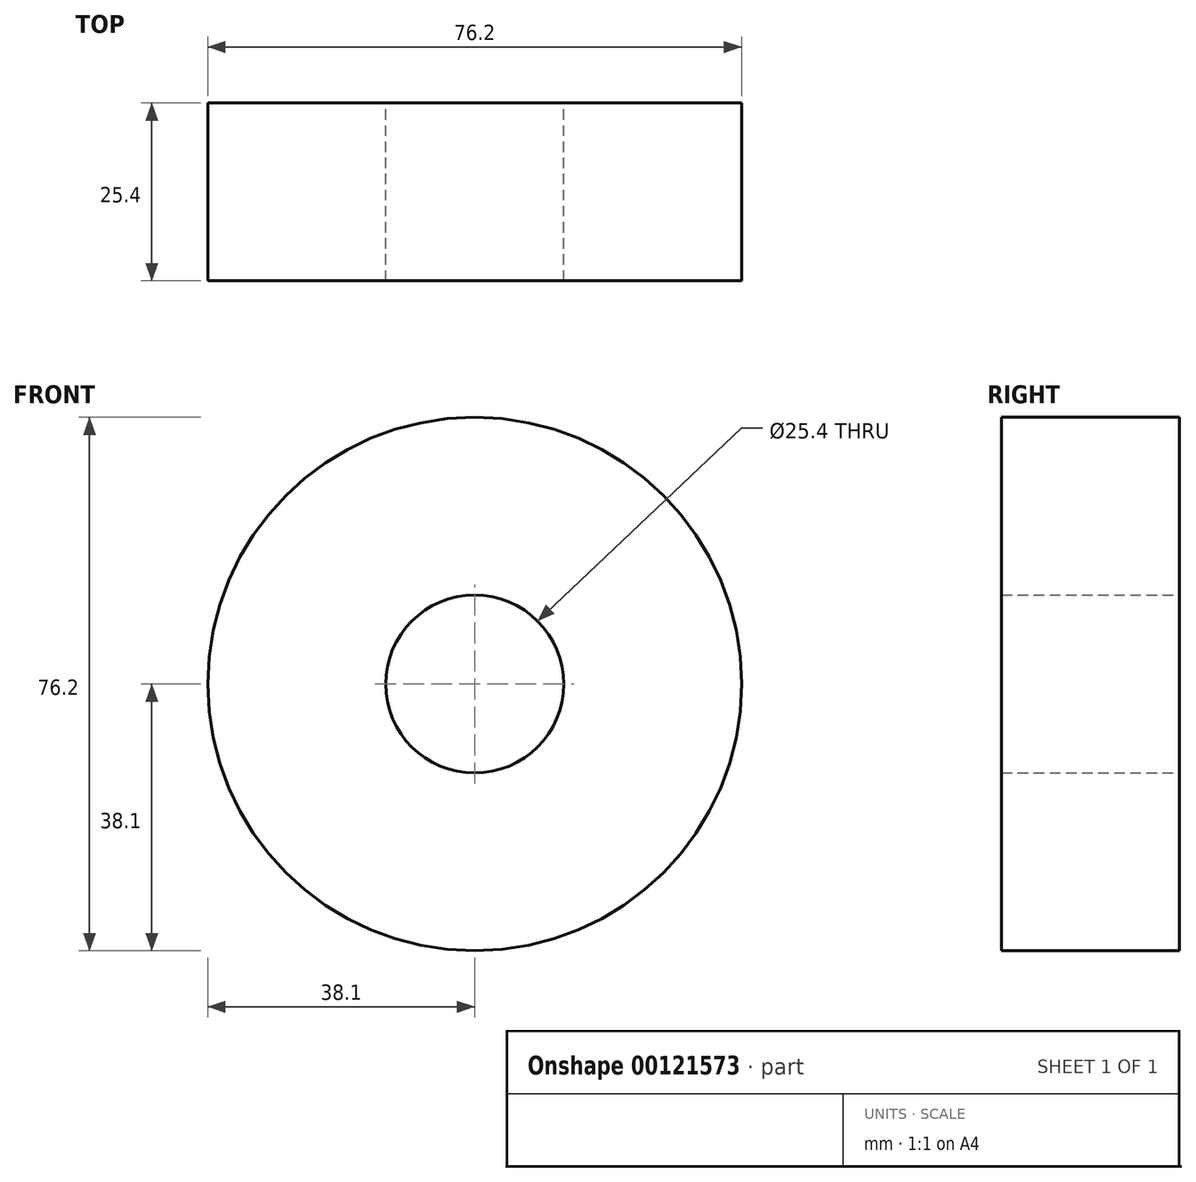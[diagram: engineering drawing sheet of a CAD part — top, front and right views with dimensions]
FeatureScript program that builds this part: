
annotation { "Feature Type Name" : "Feature", "Feature Type Description" : "" }
export const myFeature = defineFeature(function(context is Context, id is Id, definition is map)
    precondition{}
    {
        {
            var Q0;
            Q0=qCreatedBy(makeId("Front.planeOp"),FACE);
            var sketch = newSketch(context, id + "F0", { "sketchPlane" : qUnion([Q0])});
            skCircle(sketch, "E0", {"center": v(0, 0) * mm, "radius": 12.7 * mm});
            skCircle(sketch, "E1", {"center": v(0, 0) * mm, "radius": 38.1 * mm});
            skSolve(sketch);
        }
        {
            var Q0;
            Q0=makeQuery(id+"F0.imprint","IMPRINT",FACE,{"disambiguationData":[TD([[makeQuery(id+"F0.imprint","IMPRINT",EDGE,{"derivedFrom":sQuery(id+"F0.wireOp",EDGE,"E0")}),-1.0]])]});
            extrude(context, id + "F1", {"entities" : qUnion([Q0]), "depth" : 25.4 * mm});
        }
    });
